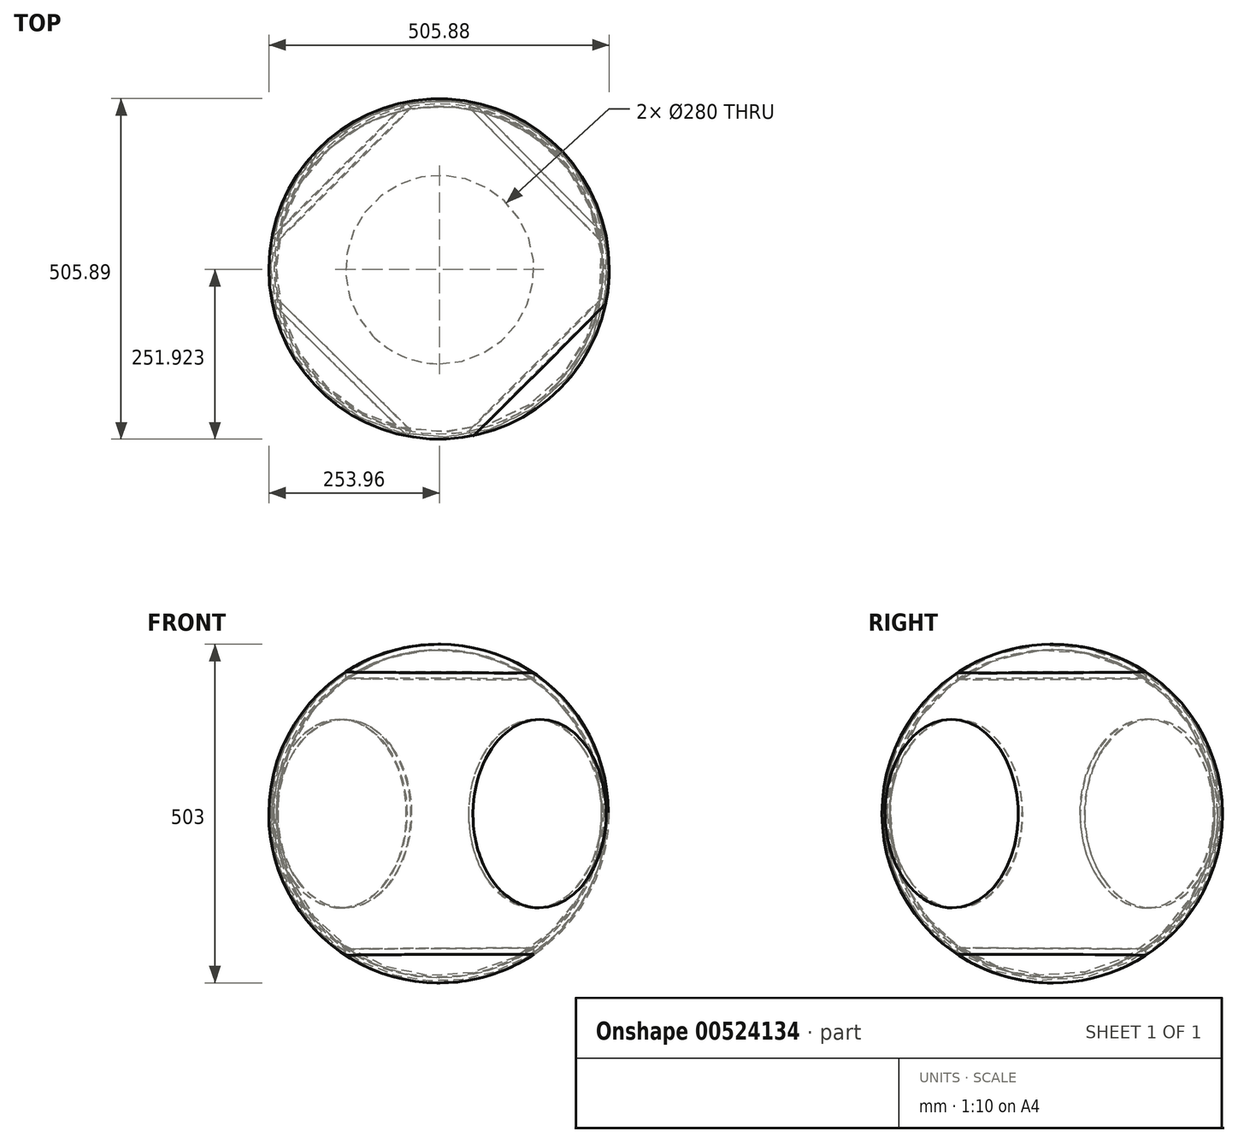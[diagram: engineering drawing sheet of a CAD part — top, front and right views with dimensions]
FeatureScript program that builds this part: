
annotation { "Feature Type Name" : "Feature", "Feature Type Description" : "" }
export const myFeature = defineFeature(function(context is Context, id is Id, definition is map)
    precondition{}
    {
        {
            var Q0;
            Q0=qCreatedBy(makeId("Right.planeOp"),FACE);
            var sketch = newSketch(context, id + "F0", { "sketchPlane" : qUnion([Q0])});
            skCircle(sketch, "E0", {"center": v(0, 0) * mm, "radius": 243.58 * mm});
            skLineSegment(sketch, "E1", {"start": v(1.44, 243.58) * mm, "end": v(1.44, -243.58) * mm});
            skCircle(sketch, "E2", {"center": v(0, 0) * mm, "radius": 251.5 * mm});
            skLineSegment(sketch, "E3", {"start": v(1.44, 243.58) * mm, "end": v(1.44, -357.35) * mm});
            skLineSegment(sketch, "E4", {"start": v(1.44, -357.35) * mm, "end": v(1.44, 517.62) * mm});
            skSolve(sketch);
        }
        {
            var Q0;
            {var subQ0=sQuery(id+"F0.wireOp",EDGE,"E4");var subQ1=sQuery(id+"F0.wireOp",EDGE,"E0");var subQ2=makeQuery(id+"F0.imprint","INTERSECT",VERTEX,{"disambiguationData":[OD(0.0)],"derivedFrom":[subQ1,subQ0]});Q0=makeQuery(id+"F0.imprint","IMPRINT",FACE,{"disambiguationData":[TD([[makeQuery(id+"F0.imprint","IMPRINT",EDGE,{"disambiguationData":[TD([[subQ2,-1.0]])],"derivedFrom":subQ1}),-1.0]])]});}
            var Q1;
            Q1=sQuery(id+"F0.wireOp",EDGE,"E4");
            revolve(context, id + "F1", {"entities" : qUnion([Q0]), "axis" : qUnion([Q1]), "revolveType" : RevolveType.FULL});
        }
        {
            var Q0;
            Q0=qCreatedBy(makeId("Top.planeOp"),FACE);
            var sketch = newSketch(context, id + "F2", { "sketchPlane" : qUnion([Q0])});
            skCircle(sketch, "E5", {"center": v(0, 0) * mm, "radius": 140 * mm});
            skLineSegment(sketch, "E6", {"start": v(0, -77.93) * mm, "end": v(0, 75.7) * mm});
            skLineSegment(sketch, "E7", {"start": v(-72.82, 0) * mm, "end": v(75.83, 0) * mm});
            skSolve(sketch);
        }
        {
            var Q0;
            Q0=qSketchRegion(id+"F2",true);
            var Q1;
            Q1=sQuery(id+"F2.wireOp",EDGE,"E5");
            extrude(context, id + "F3", {"entities" : qUnion([Q0]), "operationType" : NewBodyOperationType.INTERSECT, "surfaceEntities" : qUnion([Q1]), "endBound" : BoundingType.THROUGH_ALL, "oppositeDirection" : true, "depth" : 250 * mm});
        }
        {
            var Q0;
            Q0=makeQuery(id+"F1.opRevolve","SWEPT_BODY",BODY,{"disambiguationData":[OSD([sQuery(id+"F0.wireOp",EDGE,"E0"),sQuery(id+"F0.wireOp",EDGE,"E2"),sQuery(id+"F0.wireOp",EDGE,"E4")])]});
            var Q1;
            Q1=qCreatedBy(makeId("Top.planeOp"),FACE);
            mirror(context, id + "F4", {"entities" : qUnion([Q0]), "mirrorPlane" : qUnion([Q1])});
        }
        {
            var Q0;
            Q0=makeQuery(id+"F4.opPattern","COPY",BODY,{"derivedFrom":makeQuery(id+"F1.opRevolve","SWEPT_BODY",BODY,{"disambiguationData":[OSD([sQuery(id+"F0.wireOp",EDGE,"E0"),sQuery(id+"F0.wireOp",EDGE,"E2"),sQuery(id+"F0.wireOp",EDGE,"E4")])]}),"instanceName":"1"});
            var Q1;
            Q1=makeQuery(id+"F1.opRevolve","SWEPT_BODY",BODY,{"disambiguationData":[OSD([sQuery(id+"F0.wireOp",EDGE,"E0"),sQuery(id+"F0.wireOp",EDGE,"E2"),sQuery(id+"F0.wireOp",EDGE,"E4")])]});
            var Q2;
            Q2=qCreatedBy(makeId("Top.planeOp"),FACE);
            mirror(context, id + "F5", {"entities" : qUnion([Q0, Q1]), "mirrorPlane" : qUnion([Q2])});
        }
        {
            var Q0;
            Q0=makeQuery(id+"F5.opPattern","COPY",BODY,{"derivedFrom":makeQuery(id+"F1.opRevolve","SWEPT_BODY",BODY,{"disambiguationData":[OSD([sQuery(id+"F0.wireOp",EDGE,"E0"),sQuery(id+"F0.wireOp",EDGE,"E2"),sQuery(id+"F0.wireOp",EDGE,"E4")])]}),"instanceName":"1"});
            var Q1;
            Q1=makeQuery(id+"F5.opPattern","COPY",BODY,{"derivedFrom":makeQuery(id+"F4.opPattern","COPY",BODY,{"derivedFrom":makeQuery(id+"F1.opRevolve","SWEPT_BODY",BODY,{"disambiguationData":[OSD([sQuery(id+"F0.wireOp",EDGE,"E0"),sQuery(id+"F0.wireOp",EDGE,"E2"),sQuery(id+"F0.wireOp",EDGE,"E4")])]}),"instanceName":"1"}),"instanceName":"1"});
            var Q2;
            Q2=qCreatedBy(makeId("Origin.pointOp"),VERTEX);
            var Q3;
            Q3=sQuery(id+"F2.wireOp",EDGE,"E6");
            transform(context, id + "F6", {"entities" : qUnion([Q0, Q1]), "transformType" : TransformType.ROTATION, "transformAxis" : qUnion([Q3]), "angle" : 90 * degree, "makeCopy" : true});
        }
        {
            var Q0;
            Q0=makeQuery(id+"F4.opPattern","COPY",BODY,{"derivedFrom":makeQuery(id+"F1.opRevolve","SWEPT_BODY",BODY,{"disambiguationData":[OSD([sQuery(id+"F0.wireOp",EDGE,"E0"),sQuery(id+"F0.wireOp",EDGE,"E2"),sQuery(id+"F0.wireOp",EDGE,"E4")])]}),"instanceName":"1"});
            var Q1;
            Q1=makeQuery(id+"F5.opPattern","COPY",BODY,{"derivedFrom":makeQuery(id+"F4.opPattern","COPY",BODY,{"derivedFrom":makeQuery(id+"F1.opRevolve","SWEPT_BODY",BODY,{"disambiguationData":[OSD([sQuery(id+"F0.wireOp",EDGE,"E0"),sQuery(id+"F0.wireOp",EDGE,"E2"),sQuery(id+"F0.wireOp",EDGE,"E4")])]}),"instanceName":"1"}),"instanceName":"1"});
            var Q2;
            Q2=sQuery(id+"F2.wireOp",EDGE,"E7");
            transform(context, id + "F7", {"entities" : qUnion([Q0, Q1]), "transformType" : TransformType.ROTATION, "transformAxis" : qUnion([Q2]), "angle" : 90 * degree, "makeCopy" : false});
        }
        {
            var Q0;
            {var subQ0=sQuery(id+"F0.wireOp",EDGE,"E4");var subQ1=sQuery(id+"F0.wireOp",EDGE,"E0");var subQ2=makeQuery(id+"F0.imprint","INTERSECT",VERTEX,{"disambiguationData":[OD(0.0)],"derivedFrom":[subQ1,subQ0]});Q0=makeQuery(id+"F0.imprint","IMPRINT",FACE,{"disambiguationData":[TD([[makeQuery(id+"F0.imprint","IMPRINT",EDGE,{"disambiguationData":[TD([[subQ2,-1.0]])],"derivedFrom":subQ1}),-1.0]])]});}
            var Q1;
            Q1=sQuery(id+"F0.wireOp",EDGE,"E3");
            revolve(context, id + "F8", {"entities" : qUnion([Q0]), "axis" : qUnion([Q1]), "revolveType" : RevolveType.FULL});
        }
        {
            var Q0;
            Q0=makeQuery(id+"F6.opPattern","COPY",BODY,{"derivedFrom":makeQuery(id+"F5.opPattern","COPY",BODY,{"derivedFrom":makeQuery(id+"F1.opRevolve","SWEPT_BODY",BODY,{"disambiguationData":[OSD([sQuery(id+"F0.wireOp",EDGE,"E0"),sQuery(id+"F0.wireOp",EDGE,"E2"),sQuery(id+"F0.wireOp",EDGE,"E4")])]}),"instanceName":"1"}),"instanceName":"1"});
            var Q1;
            Q1=makeQuery(id+"F6.opPattern","COPY",BODY,{"derivedFrom":makeQuery(id+"F5.opPattern","COPY",BODY,{"derivedFrom":makeQuery(id+"F4.opPattern","COPY",BODY,{"derivedFrom":makeQuery(id+"F1.opRevolve","SWEPT_BODY",BODY,{"disambiguationData":[OSD([sQuery(id+"F0.wireOp",EDGE,"E0"),sQuery(id+"F0.wireOp",EDGE,"E2"),sQuery(id+"F0.wireOp",EDGE,"E4")])]}),"instanceName":"1"}),"instanceName":"1"}),"instanceName":"1"});
            var Q2;
            Q2=makeQuery(id+"F5.opPattern","COPY",BODY,{"derivedFrom":makeQuery(id+"F4.opPattern","COPY",BODY,{"derivedFrom":makeQuery(id+"F1.opRevolve","SWEPT_BODY",BODY,{"disambiguationData":[OSD([sQuery(id+"F0.wireOp",EDGE,"E0"),sQuery(id+"F0.wireOp",EDGE,"E2"),sQuery(id+"F0.wireOp",EDGE,"E4")])]}),"instanceName":"1"}),"instanceName":"1"});
            var Q3;
            Q3=makeQuery(id+"F5.opPattern","COPY",BODY,{"derivedFrom":makeQuery(id+"F1.opRevolve","SWEPT_BODY",BODY,{"disambiguationData":[OSD([sQuery(id+"F0.wireOp",EDGE,"E0"),sQuery(id+"F0.wireOp",EDGE,"E2"),sQuery(id+"F0.wireOp",EDGE,"E4")])]}),"instanceName":"1"});
            var Q4;
            Q4=makeQuery(id+"F4.opPattern","COPY",BODY,{"derivedFrom":makeQuery(id+"F1.opRevolve","SWEPT_BODY",BODY,{"disambiguationData":[OSD([sQuery(id+"F0.wireOp",EDGE,"E0"),sQuery(id+"F0.wireOp",EDGE,"E2"),sQuery(id+"F0.wireOp",EDGE,"E4")])]}),"instanceName":"1"});
            var Q5;
            Q5=makeQuery(id+"F1.opRevolve","SWEPT_BODY",BODY,{"disambiguationData":[OSD([sQuery(id+"F0.wireOp",EDGE,"E0"),sQuery(id+"F0.wireOp",EDGE,"E2"),sQuery(id+"F0.wireOp",EDGE,"E4")])]});
            var Q6;
            Q6=sQuery(id+"F0.wireOp",EDGE,"E4");
            transform(context, id + "F9", {"entities" : qUnion([Q0, Q1, Q2, Q3, Q4, Q5]), "transformType" : TransformType.ROTATION, "transformAxis" : qUnion([Q6]), "angle" : 45 * degree, "makeCopy" : false});
        }
    });
